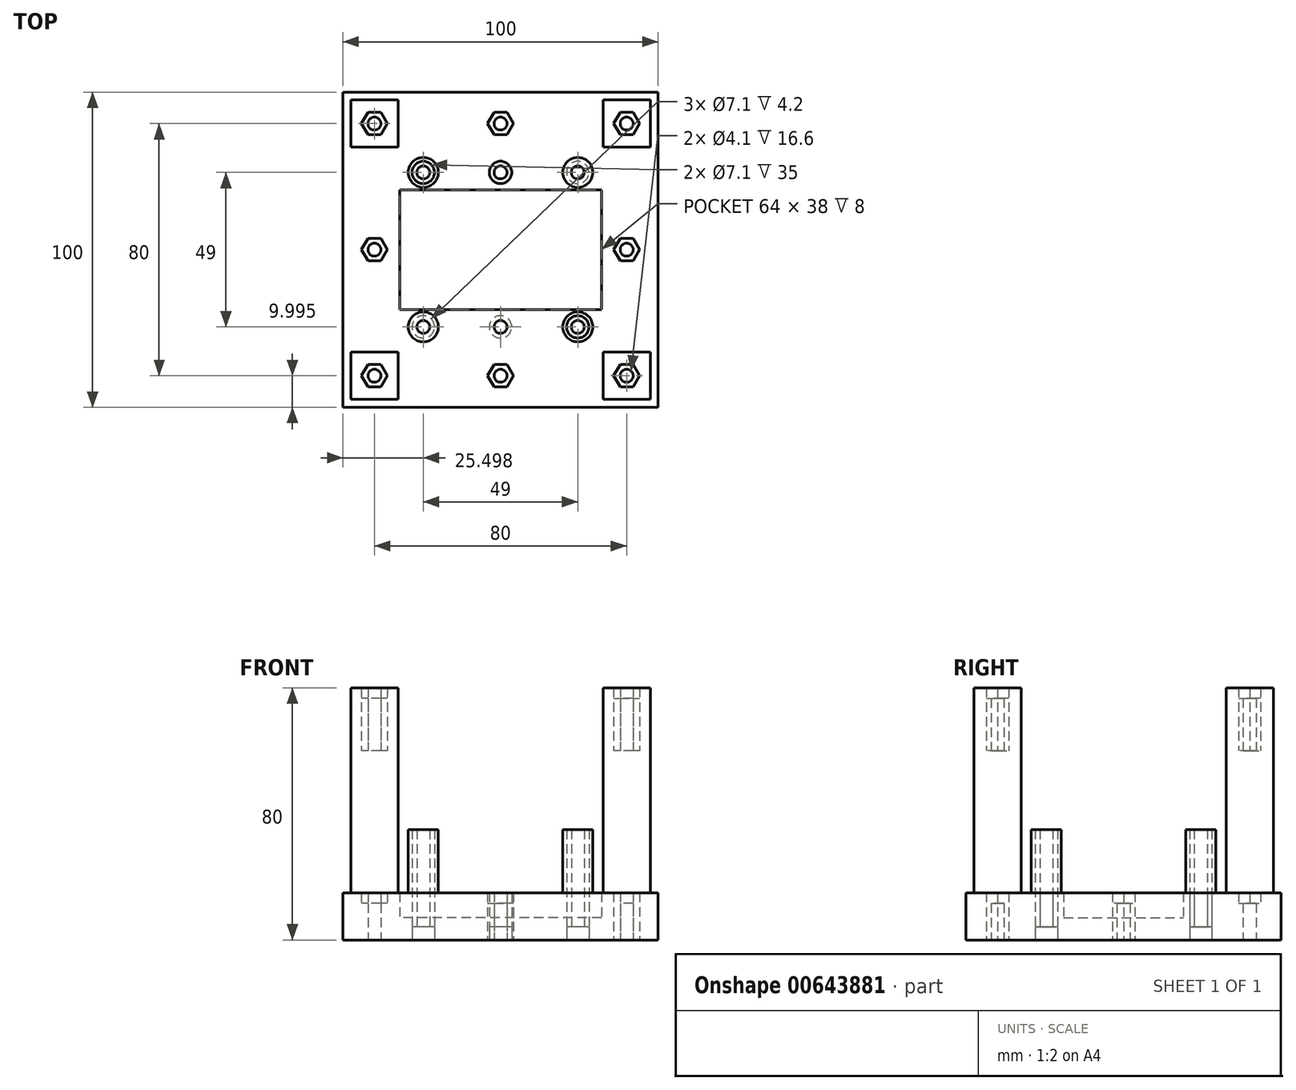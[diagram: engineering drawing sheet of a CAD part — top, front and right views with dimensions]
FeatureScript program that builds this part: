
annotation { "Feature Type Name" : "Feature", "Feature Type Description" : "" }
export const myFeature = defineFeature(function(context is Context, id is Id, definition is map)
    precondition{}
    {
        {
            var Q0;
            Q0=qCreatedBy(makeId("Top.planeOp"),FACE);
            var sketch = newSketch(context, id + "F0", { "sketchPlane" : qUnion([Q0])});
            skPoint(sketch, "E0.middle", {"position": v(0, -0.01) * mm});
            skCircle(sketch, "E1", {"center": v(-24.5, -24.51) * mm, "radius": 4.76 * mm});
            skCircle(sketch, "E2", {"center": v(24.5, -24.51) * mm, "radius": 4.76 * mm});
            skCircle(sketch, "E3", {"center": v(24.5, 24.49) * mm, "radius": 4.76 * mm});
            skCircle(sketch, "E4", {"center": v(-24.5, 24.49) * mm, "radius": 4.76 * mm});
            skLineSegment(sketch, "E5.bottom", {"start": v(32, -19.01) * mm, "end": v(-32, -19.01) * mm});
            skLineSegment(sketch, "E5.top", {"start": v(32, 18.99) * mm, "end": v(-32, 18.99) * mm});
            skLineSegment(sketch, "E5.left", {"start": v(32, -19.01) * mm, "end": v(32, 18.99) * mm});
            skLineSegment(sketch, "E5.right", {"start": v(-32, -19.01) * mm, "end": v(-32, 18.99) * mm});
            skCircle(sketch, "E6", {"center": v(-40, 39.99) * mm, "radius": 2.05 * mm});
            skCircle(sketch, "E7", {"center": v(-40, -0.01) * mm, "radius": 2.05 * mm});
            skCircle(sketch, "E8", {"center": v(0, 39.99) * mm, "radius": 2.05 * mm});
            skCircle(sketch, "E9", {"center": v(-24.5, -24.51) * mm, "radius": 2.05 * mm});
            skCircle(sketch, "E10.MirrorC", {"center": v(24.5, -24.51) * mm, "radius": 2.05 * mm});
            skCircle(sketch, "E11.MirrorC", {"center": v(24.5, 24.49) * mm, "radius": 2.05 * mm});
            skCircle(sketch, "E12.MirrorC", {"center": v(-24.5, 24.49) * mm, "radius": 2.05 * mm});
            skCircle(sketch, "E13.MirrorC", {"center": v(-40, -40.01) * mm, "radius": 2.05 * mm});
            skCircle(sketch, "E14.MirrorC", {"center": v(40, -40.01) * mm, "radius": 2.05 * mm});
            skCircle(sketch, "E15.MirrorC", {"center": v(40, 39.99) * mm, "radius": 2.05 * mm});
            skCircle(sketch, "E16.MirrorC", {"center": v(40, -0.01) * mm, "radius": 2.05 * mm});
            skCircle(sketch, "E17.MirrorC", {"center": v(0, -40.01) * mm, "radius": 2.05 * mm});
            skCircle(sketch, "E18", {"center": v(-24.5, -24.51) * mm, "radius": 3.55 * mm});
            skCircle(sketch, "E19.MirrorC", {"center": v(24.5, -24.51) * mm, "radius": 3.55 * mm});
            skCircle(sketch, "E20.MirrorC", {"center": v(24.5, 24.49) * mm, "radius": 3.55 * mm});
            skCircle(sketch, "E21.MirrorC", {"center": v(-24.5, 24.49) * mm, "radius": 3.55 * mm});
            skLineSegment(sketch, "E22.0", {"start": v(-50, -50.01) * mm, "end": v(-50, 49.99) * mm});
            skLineSegment(sketch, "E23.0", {"start": v(50, -50.01) * mm, "end": v(50, 49.99) * mm});
            skLineSegment(sketch, "E24.0", {"start": v(-50, 49.99) * mm, "end": v(50, 49.99) * mm});
            skLineSegment(sketch, "E25", {"start": v(-50, -50.01) * mm, "end": v(50, -50.01) * mm});
            skLineSegment(sketch, "E26.bottom", {"start": v(-32.5, -47.51) * mm, "end": v(-47.5, -47.51) * mm});
            skLineSegment(sketch, "E26.top", {"start": v(-32.5, -32.51) * mm, "end": v(-47.5, -32.51) * mm});
            skLineSegment(sketch, "E26.left", {"start": v(-32.5, -47.51) * mm, "end": v(-32.5, -32.51) * mm});
            skLineSegment(sketch, "E26.right", {"start": v(-47.5, -47.51) * mm, "end": v(-47.5, -32.51) * mm});
            skLineSegment(sketch, "E27.MirrorCS", {"start": v(32.5, -47.51) * mm, "end": v(47.5, -47.51) * mm});
            skLineSegment(sketch, "E28.MirrorCS", {"start": v(32.5, -47.51) * mm, "end": v(32.5, -32.51) * mm});
            skLineSegment(sketch, "E29.MirrorCS", {"start": v(32.5, -32.51) * mm, "end": v(47.5, -32.51) * mm});
            skLineSegment(sketch, "E30.MirrorCS", {"start": v(47.5, -47.51) * mm, "end": v(47.5, -32.51) * mm});
            skLineSegment(sketch, "E31.MirrorCS", {"start": v(47.5, 47.49) * mm, "end": v(47.5, 32.49) * mm});
            skLineSegment(sketch, "E32.MirrorCS", {"start": v(32.5, 32.49) * mm, "end": v(47.5, 32.49) * mm});
            skLineSegment(sketch, "E33.MirrorCS", {"start": v(32.5, 47.49) * mm, "end": v(47.5, 47.49) * mm});
            skLineSegment(sketch, "E34.MirrorCS", {"start": v(32.5, 47.49) * mm, "end": v(32.5, 32.49) * mm});
            skLineSegment(sketch, "E35.MirrorCS", {"start": v(-32.5, 47.49) * mm, "end": v(-47.5, 47.49) * mm});
            skLineSegment(sketch, "E36.MirrorCS", {"start": v(-32.5, 47.49) * mm, "end": v(-32.5, 32.49) * mm});
            skLineSegment(sketch, "E37.MirrorCS", {"start": v(-47.5, 47.49) * mm, "end": v(-47.5, 32.49) * mm});
            skLineSegment(sketch, "E38.MirrorCS", {"start": v(-32.5, 32.49) * mm, "end": v(-47.5, 32.49) * mm});
            skLineSegment(sketch, "E39.0", {"start": v(-37.95, -43.56) * mm, "end": v(-42.05, -43.56) * mm});
            skLineSegment(sketch, "E39.1", {"start": v(-42.05, -43.56) * mm, "end": v(-44.1, -40.01) * mm});
            skLineSegment(sketch, "E39.2", {"start": v(-44.1, -40.01) * mm, "end": v(-42.05, -36.46) * mm});
            skLineSegment(sketch, "E39.3", {"start": v(-42.05, -36.46) * mm, "end": v(-37.95, -36.46) * mm});
            skLineSegment(sketch, "E39.4", {"start": v(-37.95, -36.46) * mm, "end": v(-35.9, -40.01) * mm});
            skLineSegment(sketch, "E39.5", {"start": v(-35.9, -40.01) * mm, "end": v(-37.95, -43.56) * mm});
            skLineSegment(sketch, "E40.MirrorCS", {"start": v(42.05, -43.56) * mm, "end": v(44.1, -40.01) * mm});
            skLineSegment(sketch, "E41.MirrorCS", {"start": v(37.95, -43.56) * mm, "end": v(42.05, -43.56) * mm});
            skLineSegment(sketch, "E42.MirrorCS", {"start": v(44.1, -40.01) * mm, "end": v(42.05, -36.46) * mm});
            skLineSegment(sketch, "E43.MirrorCS", {"start": v(35.9, -40.01) * mm, "end": v(37.95, -43.56) * mm});
            skLineSegment(sketch, "E44.MirrorCS", {"start": v(42.05, -36.46) * mm, "end": v(37.95, -36.46) * mm});
            skLineSegment(sketch, "E45.MirrorCS", {"start": v(37.95, -36.46) * mm, "end": v(35.9, -40.01) * mm});
            skLineSegment(sketch, "E46.MirrorCS", {"start": v(37.95, 36.44) * mm, "end": v(35.9, 39.99) * mm});
            skLineSegment(sketch, "E47.MirrorCS", {"start": v(44.1, 39.99) * mm, "end": v(42.05, 36.44) * mm});
            skLineSegment(sketch, "E48.MirrorCS", {"start": v(35.9, 39.99) * mm, "end": v(37.95, 43.54) * mm});
            skLineSegment(sketch, "E49.MirrorCS", {"start": v(42.05, 36.44) * mm, "end": v(37.95, 36.44) * mm});
            skLineSegment(sketch, "E50.MirrorCS", {"start": v(42.05, 43.54) * mm, "end": v(44.1, 39.99) * mm});
            skLineSegment(sketch, "E51.MirrorCS", {"start": v(37.95, 43.54) * mm, "end": v(42.05, 43.54) * mm});
            skLineSegment(sketch, "E52.MirrorCS", {"start": v(-37.95, 43.54) * mm, "end": v(-42.05, 43.54) * mm});
            skLineSegment(sketch, "E53.MirrorCS", {"start": v(-35.9, 39.99) * mm, "end": v(-37.95, 43.54) * mm});
            skLineSegment(sketch, "E54.MirrorCS", {"start": v(-42.05, 36.44) * mm, "end": v(-37.95, 36.44) * mm});
            skLineSegment(sketch, "E55.MirrorCS", {"start": v(-42.05, 43.54) * mm, "end": v(-44.1, 39.99) * mm});
            skLineSegment(sketch, "E56.MirrorCS", {"start": v(-44.1, 39.99) * mm, "end": v(-42.05, 36.44) * mm});
            skLineSegment(sketch, "E57.MirrorCS", {"start": v(-37.95, 36.44) * mm, "end": v(-35.9, 39.99) * mm});
            skLineSegment(sketch, "E58.0", {"start": v(2.05, -43.56) * mm, "end": v(-2.05, -43.56) * mm});
            skLineSegment(sketch, "E58.1", {"start": v(-2.05, -43.56) * mm, "end": v(-4.1, -40.01) * mm});
            skLineSegment(sketch, "E58.2", {"start": v(-4.1, -40.01) * mm, "end": v(-2.05, -36.46) * mm});
            skLineSegment(sketch, "E58.3", {"start": v(-2.05, -36.46) * mm, "end": v(2.05, -36.46) * mm});
            skLineSegment(sketch, "E58.4", {"start": v(2.05, -36.46) * mm, "end": v(4.1, -40.01) * mm});
            skLineSegment(sketch, "E58.5", {"start": v(4.1, -40.01) * mm, "end": v(2.05, -43.56) * mm});
            skLineSegment(sketch, "E59.MirrorCS", {"start": v(2.05, 36.44) * mm, "end": v(4.1, 39.99) * mm});
            skLineSegment(sketch, "E60.MirrorCS", {"start": v(-2.05, 43.54) * mm, "end": v(-4.1, 39.99) * mm});
            skLineSegment(sketch, "E61.MirrorCS", {"start": v(-2.05, 36.44) * mm, "end": v(2.05, 36.44) * mm});
            skLineSegment(sketch, "E62.MirrorCS", {"start": v(4.1, 39.99) * mm, "end": v(2.05, 43.54) * mm});
            skLineSegment(sketch, "E63.MirrorCS", {"start": v(2.05, 43.54) * mm, "end": v(-2.05, 43.54) * mm});
            skLineSegment(sketch, "E64.MirrorCS", {"start": v(-4.1, 39.99) * mm, "end": v(-2.05, 36.44) * mm});
            skLineSegment(sketch, "E65.0", {"start": v(-37.95, -3.56) * mm, "end": v(-42.05, -3.56) * mm});
            skLineSegment(sketch, "E65.1", {"start": v(-42.05, -3.56) * mm, "end": v(-44.1, -0.01) * mm});
            skLineSegment(sketch, "E65.2", {"start": v(-44.1, -0.01) * mm, "end": v(-42.05, 3.54) * mm});
            skLineSegment(sketch, "E65.3", {"start": v(-42.05, 3.54) * mm, "end": v(-37.95, 3.54) * mm});
            skLineSegment(sketch, "E65.4", {"start": v(-37.95, 3.54) * mm, "end": v(-35.9, -0.01) * mm});
            skLineSegment(sketch, "E65.5", {"start": v(-35.9, -0.01) * mm, "end": v(-37.95, -3.56) * mm});
            skLineSegment(sketch, "E66.MirrorCS", {"start": v(37.95, -3.56) * mm, "end": v(42.05, -3.56) * mm});
            skLineSegment(sketch, "E67.MirrorCS", {"start": v(42.05, 3.54) * mm, "end": v(37.95, 3.54) * mm});
            skLineSegment(sketch, "E68.MirrorCS", {"start": v(42.05, -3.56) * mm, "end": v(44.1, -0.01) * mm});
            skLineSegment(sketch, "E69.MirrorCS", {"start": v(44.1, -0.01) * mm, "end": v(42.05, 3.54) * mm});
            skLineSegment(sketch, "E70.MirrorCS", {"start": v(35.9, -0.01) * mm, "end": v(37.95, -3.56) * mm});
            skLineSegment(sketch, "E71.MirrorCS", {"start": v(37.95, 3.54) * mm, "end": v(35.9, -0.01) * mm});
            skCircle(sketch, "E72", {"center": v(0, -24.51) * mm, "radius": 2.05 * mm});
            skCircle(sketch, "E73", {"center": v(0, -24.51) * mm, "radius": 3.55 * mm});
            skCircle(sketch, "E74.MirrorC", {"center": v(0, 24.49) * mm, "radius": 2.05 * mm});
            skCircle(sketch, "E75.MirrorC", {"center": v(0, 24.49) * mm, "radius": 3.55 * mm});
            skSolve(sketch);
        }
        {
            var Q0;
            Q0=makeQuery(id+"F0.imprint","IMPRINT",FACE,{"disambiguationData":[TD([[makeQuery(id+"F0.imprint","IMPRINT",EDGE,{"derivedFrom":sQuery(id+"F0.wireOp",EDGE,"E1")}),-1.0]])]});
            extrude(context, id + "F1", {"entities" : qUnion([Q0]), "depth" : 15 * mm, "offsetDistance" : 25.4 * mm});
        }
        {
            var Q0;
            Q0=makeQuery(id+"F0.imprint","IMPRINT",FACE,{"disambiguationData":[TD([[makeQuery(id+"F0.imprint","IMPRINT",EDGE,{"derivedFrom":sQuery(id+"F0.wireOp",EDGE,"E26.bottom")}),-1.0]])]});
            var Q1;
            Q1=makeQuery(id+"F0.imprint","IMPRINT",FACE,{"disambiguationData":[TD([[makeQuery(id+"F0.imprint","IMPRINT",EDGE,{"derivedFrom":sQuery(id+"F0.wireOp",EDGE,"E27.MirrorCS")}),1.0]])]});
            var Q2;
            Q2=makeQuery(id+"F0.imprint","IMPRINT",FACE,{"disambiguationData":[TD([[makeQuery(id+"F0.imprint","IMPRINT",EDGE,{"derivedFrom":sQuery(id+"F0.wireOp",EDGE,"E35.MirrorCS")}),1.0]])]});
            var Q3;
            Q3=makeQuery(id+"F0.imprint","IMPRINT",FACE,{"disambiguationData":[TD([[makeQuery(id+"F0.imprint","IMPRINT",EDGE,{"derivedFrom":sQuery(id+"F0.wireOp",EDGE,"E31.MirrorCS")}),-1.0]])]});
            extrude(context, id + "F2", {"entities" : qUnion([Q0, Q1, Q2, Q3]), "operationType" : NewBodyOperationType.ADD, "depth" : 80 * mm, "offsetDistance" : 25.4 * mm});
        }
        {
            var Q0;
            Q0=makeQuery(id+"F0.imprint","IMPRINT",FACE,{"disambiguationData":[TD([[makeQuery(id+"F0.imprint","IMPRINT",EDGE,{"derivedFrom":sQuery(id+"F0.wireOp",EDGE,"E6")}),-1.0]])]});
            var Q1;
            Q1=makeQuery(id+"F0.imprint","IMPRINT",FACE,{"disambiguationData":[TD([[makeQuery(id+"F0.imprint","IMPRINT",EDGE,{"derivedFrom":sQuery(id+"F0.wireOp",EDGE,"E15.MirrorC")}),1.0]])]});
            var Q2;
            Q2=makeQuery(id+"F0.imprint","IMPRINT",FACE,{"disambiguationData":[TD([[makeQuery(id+"F0.imprint","IMPRINT",EDGE,{"derivedFrom":sQuery(id+"F0.wireOp",EDGE,"E14.MirrorC")}),-1.0]])]});
            var Q3;
            Q3=makeQuery(id+"F0.imprint","IMPRINT",FACE,{"disambiguationData":[TD([[makeQuery(id+"F0.imprint","IMPRINT",EDGE,{"derivedFrom":sQuery(id+"F0.wireOp",EDGE,"E13.MirrorC")}),1.0]])]});
            extrude(context, id + "F3", {"entities" : qUnion([Q0, Q1, Q2, Q3]), "operationType" : NewBodyOperationType.ADD, "depth" : 76.6 * mm, "offsetDistance" : 25.4 * mm});
        }
        {
            var Q0;
            Q0=makeQuery(id+"F0.imprint","IMPRINT",FACE,{"disambiguationData":[TD([[makeQuery(id+"F0.imprint","IMPRINT",EDGE,{"derivedFrom":sQuery(id+"F0.wireOp",EDGE,"E5.bottom")}),-1.0]])]});
            extrude(context, id + "F4", {"entities" : qUnion([Q0]), "operationType" : NewBodyOperationType.ADD, "depth" : 7 * mm, "offsetDistance" : 25.4 * mm});
        }
        {
            var Q0;
            Q0=makeQuery(id+"F0.imprint","IMPRINT",FACE,{"disambiguationData":[TD([[makeQuery(id+"F0.imprint","IMPRINT",EDGE,{"derivedFrom":sQuery(id+"F0.wireOp",EDGE,"E7")}),-1.0]])]});
            var Q1;
            Q1=makeQuery(id+"F0.imprint","IMPRINT",FACE,{"disambiguationData":[TD([[makeQuery(id+"F0.imprint","IMPRINT",EDGE,{"derivedFrom":sQuery(id+"F0.wireOp",EDGE,"E17.MirrorC")}),1.0]])]});
            var Q2;
            Q2=makeQuery(id+"F0.imprint","IMPRINT",FACE,{"disambiguationData":[TD([[makeQuery(id+"F0.imprint","IMPRINT",EDGE,{"derivedFrom":sQuery(id+"F0.wireOp",EDGE,"E16.MirrorC")}),1.0]])]});
            var Q3;
            Q3=makeQuery(id+"F0.imprint","IMPRINT",FACE,{"disambiguationData":[TD([[makeQuery(id+"F0.imprint","IMPRINT",EDGE,{"derivedFrom":sQuery(id+"F0.wireOp",EDGE,"E8")}),-1.0]])]});
            extrude(context, id + "F5", {"entities" : qUnion([Q0, Q1, Q2, Q3]), "operationType" : NewBodyOperationType.ADD, "depth" : 11.6 * mm, "offsetDistance" : 25.4 * mm});
        }
        {
            var Q0;
            Q0=makeQuery(id+"F0.imprint","IMPRINT",FACE,{"disambiguationData":[TD([[makeQuery(id+"F0.imprint","IMPRINT",EDGE,{"derivedFrom":sQuery(id+"F0.wireOp",EDGE,"E4")}),1.0]])]});
            var Q1;
            Q1=makeQuery(id+"F0.imprint","IMPRINT",FACE,{"disambiguationData":[TD([[makeQuery(id+"F0.imprint","IMPRINT",EDGE,{"derivedFrom":sQuery(id+"F0.wireOp",EDGE,"E3")}),1.0]])]});
            var Q2;
            Q2=makeQuery(id+"F0.imprint","IMPRINT",FACE,{"disambiguationData":[TD([[makeQuery(id+"F0.imprint","IMPRINT",EDGE,{"derivedFrom":sQuery(id+"F0.wireOp",EDGE,"E2")}),1.0]])]});
            var Q3;
            Q3=makeQuery(id+"F0.imprint","IMPRINT",FACE,{"disambiguationData":[TD([[makeQuery(id+"F0.imprint","IMPRINT",EDGE,{"derivedFrom":sQuery(id+"F0.wireOp",EDGE,"E1")}),1.0]])]});
            extrude(context, id + "F6", {"entities" : qUnion([Q0, Q1, Q2, Q3]), "operationType" : NewBodyOperationType.ADD, "depth" : 35 * mm, "offsetDistance" : 25.4 * mm});
        }
        {
            var Q0;
            Q0=makeQuery(id+"F0.imprint","IMPRINT",FACE,{"disambiguationData":[TD([[makeQuery(id+"F0.imprint","IMPRINT",EDGE,{"derivedFrom":sQuery(id+"F0.wireOp",EDGE,"E12.MirrorC")}),1.0]])]});
            var Q1;
            Q1=makeQuery(id+"F0.imprint","IMPRINT",FACE,{"disambiguationData":[TD([[makeQuery(id+"F0.imprint","IMPRINT",EDGE,{"derivedFrom":sQuery(id+"F0.wireOp",EDGE,"E11.MirrorC")}),-1.0]])]});
            var Q2;
            Q2=makeQuery(id+"F0.imprint","IMPRINT",FACE,{"disambiguationData":[TD([[makeQuery(id+"F0.imprint","IMPRINT",EDGE,{"derivedFrom":sQuery(id+"F0.wireOp",EDGE,"E10.MirrorC")}),1.0]])]});
            var Q3;
            Q3=makeQuery(id+"F0.imprint","IMPRINT",FACE,{"disambiguationData":[TD([[makeQuery(id+"F0.imprint","IMPRINT",EDGE,{"derivedFrom":sQuery(id+"F0.wireOp",EDGE,"E9")}),-1.0]])]});
            extrude(context, id + "F7", {"entities" : qUnion([Q0, Q1, Q2, Q3]), "operationType" : NewBodyOperationType.ADD, "depth" : 35 * mm, "offsetDistance" : 25.4 * mm, "hasSecondDirection" : true, "secondDirectionOppositeDirection" : true, "secondDirectionDepth" : -4.2 * mm});
        }
        {
            var Q0;
            Q0=makeQuery(id+"F0.imprint","IMPRINT",FACE,{"disambiguationData":[TD([[makeQuery(id+"F0.imprint","IMPRINT",EDGE,{"derivedFrom":sQuery(id+"F0.wireOp",EDGE,"E72")}),-1.0]])]});
            var Q1;
            Q1=makeQuery(id+"F0.imprint","IMPRINT",FACE,{"disambiguationData":[TD([[makeQuery(id+"F0.imprint","IMPRINT",EDGE,{"derivedFrom":sQuery(id+"F0.wireOp",EDGE,"E74.MirrorC")}),1.0]])]});
            extrude(context, id + "F8", {"entities" : qUnion([Q0, Q1]), "operationType" : NewBodyOperationType.ADD, "depth" : 15 * mm, "offsetDistance" : 25.4 * mm, "hasSecondDirection" : true, "secondDirectionOppositeDirection" : true, "secondDirectionDepth" : -4.2 * mm});
        }
        {
            var Q0;
            Q0=makeQuery(id+"F0.imprint","IMPRINT",FACE,{"disambiguationData":[TD([[makeQuery(id+"F0.imprint","IMPRINT",EDGE,{"derivedFrom":sQuery(id+"F0.wireOp",EDGE,"E6")}),1.0]])]});
            var Q1;
            Q1=makeQuery(id+"F0.imprint","IMPRINT",FACE,{"disambiguationData":[TD([[makeQuery(id+"F0.imprint","IMPRINT",EDGE,{"derivedFrom":sQuery(id+"F0.wireOp",EDGE,"E15.MirrorC")}),-1.0]])]});
            var Q2;
            Q2=makeQuery(id+"F0.imprint","IMPRINT",FACE,{"disambiguationData":[TD([[makeQuery(id+"F0.imprint","IMPRINT",EDGE,{"derivedFrom":sQuery(id+"F0.wireOp",EDGE,"E14.MirrorC")}),1.0]])]});
            var Q3;
            Q3=makeQuery(id+"F0.imprint","IMPRINT",FACE,{"disambiguationData":[TD([[makeQuery(id+"F0.imprint","IMPRINT",EDGE,{"derivedFrom":sQuery(id+"F0.wireOp",EDGE,"E13.MirrorC")}),-1.0]])]});
            extrude(context, id + "F9", {"entities" : qUnion([Q0, Q1, Q2, Q3]), "operationType" : NewBodyOperationType.ADD, "depth" : 60 * mm, "offsetDistance" : 25.4 * mm});
        }
    });
